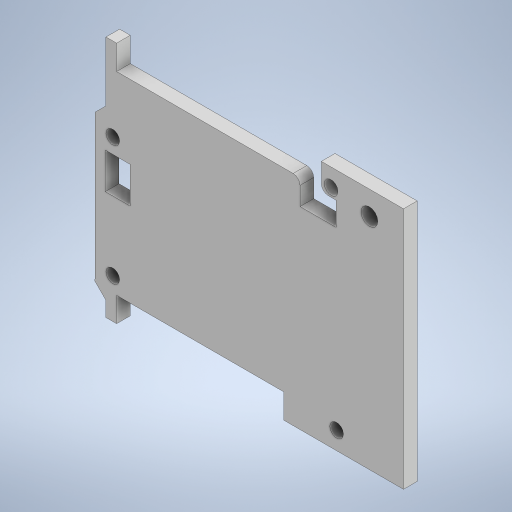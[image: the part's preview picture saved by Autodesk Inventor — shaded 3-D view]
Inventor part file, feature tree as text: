
AUTODESK INVENTOR PART (.ipt)
format: ipt  version: 2024 (Build 280153000, 153)  size: 701,440 bytes
history: native  units: in
note: dims shown in document units (in); Inventor stores cm internally (conversion verified against a paired STEP export)
features: extrude x7, sketch x6, projected_geometry x4, fillet x1
ambient origin geometry x8: Origin, YZ Plane, XZ Plane, XY Plane, X Axis, Y Axis, Z Axis, Center Point
bodies: Solid1 (feature_tree)
feature tree (18):
  extrude  "Extrusion1"  Depth=0.125in
  extrude  "Extrusion2"  Depth=0.015in
  extrude  "Extrusion3"  Depth=0.015in
  extrude  "Extrusion4"  Depth=0.005in
  extrude  "Extrusion5"  Depth=0.125in
  fillet  "Fillet1"  Radius=0.125in
  extrude  "Extrusion6"  Depth=0.125in
  extrude  "Extrusion7"  Depth=0.125in TaperAngle=0.0deg
  sketch  "Sketch3"  dims[d0=0.125in d1=0.0in d2=0.015in]
  projected_geometry  "Projected Loop1"
  sketch  "Sketch4"  dims[d3=0.015in d4=0.015in]
  projected_geometry  "Projected Loop2"
  sketch  "Sketch6"  dims[d5=0.015in d6=0.015in]
  projected_geometry  "Projected Loop3"
  sketch  "Sketch7"  dims[d7=0.015in d8=0.005in]
  projected_geometry  "Projected Loop4"
  sketch  "Sketch8"  dims[d9=1.0in d10=0.0in d11=0.125in d12=0.125in]
  sketch  "Sketch9"  dims[d13=0.125in d14=0.125in d15=0.125in d16=0.0in d17=0.125in d18=0.0in d19=0.125in d20=0.0in d21=0.063in d22=1.0in d23=0.0in d24=1.0in d25=0.0in]
